# Revit family: Adore-1
name_source: partatom
category: Furniture
units: mm (PartAtom-declared; Revit-internal decimal feet)

## family parameters
Always vertical = Yes
Cut with Voids When Loaded = No
OmniClass Number = 23.40.00.00
OmniClass Title = Equipment and Furnishings
Room Calculation Point = No
Shared = No
Work Plane-Based = No

## types (8) — shared parameters
AD2 = No
Assembly Code = E2020200
Manufacturer = Gresham Office Funiture
Model = ADORE
Range = SEATING
URL = www.gof.co.uk

## per-type parameters (varying)
| type | AD1 | AD1 & AD2 | AD11 | AD12 | AD13 | AD14 | AD3 | AD5 | Low Seat | Product Brochure | Product Data Specification | Standard Seat | Stool Seat |
| AD3 | No | No | No | No | No | No | Yes | No | No |  |  | No | Yes |
| AD1 | Yes | Yes | No | No | No | No | No | No | Yes | https://gof.co.uk | https://gof.co.uk | No | No |
| AD2 | No | Yes | No | No | No | No | No | No | Yes |  |  | No | No |
| AD5 | No | No | No | No | No | No | No | Yes | No |  |  | Yes | No |
| AD11 | No | No | Yes | No | No | No | No | No | No |  |  | Yes | No |
| AD12 | No | No | No | Yes | No | No | No | No | No |  |  | Yes | No |
| AD13 | No | No | No | No | Yes | No | No | No | No |  |  | Yes | No |
| AD14 | No | No | No | No | No | Yes | No | No | No |  |  | Yes | No |

note: column(s) folded — value = type name in every type: Product Code

## geometry (parser evidence)
native form markers: Sweep x20
no freeform markers — native parametric forms only
